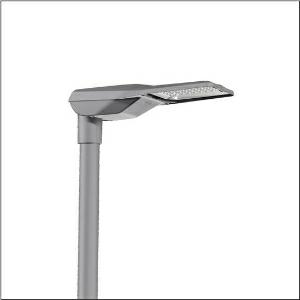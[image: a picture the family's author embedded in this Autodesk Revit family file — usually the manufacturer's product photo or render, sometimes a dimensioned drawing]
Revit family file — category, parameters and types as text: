
# Revit family: streetlight_sl_21_iq_mini___st0_5a_5xe2b41g08gb_465e
name_source: partatom
category: Lighting Fixtures
units: mm (PartAtom-declared; Revit-internal decimal feet)

## family parameters
Cut with Voids When Loaded = No
Host = Face
Light Source = No
Part Type = Normal
Room Calculation Point = No
Round Connector Dimension = Use Diameter
Shared = No

## types (1)
- --- (1 x LED, 5920 lm, 37.1 W, 4000K)
    Apparent Load = 37 VA
    CIE Flux Codes = 41 75 97 100 100
    Color Rendering = 70
    Color Temperature = 4000K
    Default Elevation = 1800 mm
    Description = Streetlight SL 21 iQ mini, mast luminaire, primary light control with lens, of PMMA, primary optical cover: cover, of toughened safety glass, transparent, light distribution: ST0.5a, light emission: direct distribution, primary light characteristic: asymmetric, installation type: post-top, side-entry, LED, High Power LED, rated luminous flux: 5.920lm, luminous efficacy: 160lm/W, light colour: 740, colour temperature: 4000K, control gear: iQ Street-Remote, control: Street-Remote, Auto-Match, Temp-Guard, Lumen-Switch, Night-Set, Smart-Wire, Light-Fading, Desk-Remote (wireless, voltage-free reading and setting of iQ features in the workshop via application-optimized NFC function/RFID function), optimised constant luminous flux control (CLO 2.0), pre-setting: linear dimming characteristic, mains connection: 220..240V, AC, 50/60Hz, start of lifetime: 37W, end of service life: 39W, reduction: 18W, luminaire housing, of diecast aluminium, powder-coated, Siteco® metallic grey (DB 702S), corrosivity category C5 mid according to DIN EN ISO 12944, please order mast flange separately, inclination adjustable: 0°, 5°, 10°, 15°, sealing non-destructively replaceable, multi-level sealing system, length: 628mm, width: 235mm, height: 110mm, mast flange for spigot size: 42mm (side-entry): 5XC10008XM4, 60/48mm (side-entry/post-top): 5XC10108XM2, 76/60mm (side-entry/post-top): 5XC10108XM1, mounting height: 4..8m, protection rating (complete): IP66, insulation class (complete): insulation class II (safety insulation), certification: CE, ENEC, ENEC+, VDE, impact resistance: IK10, permissible operating ambient temperature for outdoor applications: -40..+50°C, standard-compliant lighting for roads and squares, packaging unit: 1 piece

Light Distribution: ST0.5a
    Height = 110 mm
    Lamp = 1 x LED
    Lamp Light Flux = 5920 lm
    Lamp Power = 37.1 W
    Lamp count = 1
    Length = 625 mm
    Luminous efficacy = 160 lm/W
    Manufacturer = Siteco
    ModVariant = No
    Model = 5XE2B41G08GB
    Number of Poles = 1
    OnlyDefault = Yes
    Power Factor = 1
    Product Name = Streetlight SL 21 iQ mini | ST0.5a
    Product group = mast luminaire | pylon top
    ProductGroupID = 6100
    Protection Class = Protection class II
    Protection Degree = IP 66
    RLX_Detail_Level = 1
    RLX_Emergency_Light_Flux = 0 lm
    RLX_Emergency_Type = 0
    RLX_Emergency_Type_DB = No
    RlxData = <blob elided: 37281 chars, md5=20de013a>
    Socket = socket
    Standby Power = 0 W
    System Light Flux = 5920 lm
    System Power = 37 W
    Type Comments = factory setting: luminous flux: 100 % | dim-lin: 254 | 385 mA
    Type Image = l_1003519.jpg
    URL = http://relux.com
    VarID = @adj_212599
    Voltage = 0 V
    Weight = 0.00 kg
    Width = 234 mm

## geometry (parser evidence)
native form markers: Blend x4, Sweep x8
no freeform markers — native parametric forms only
